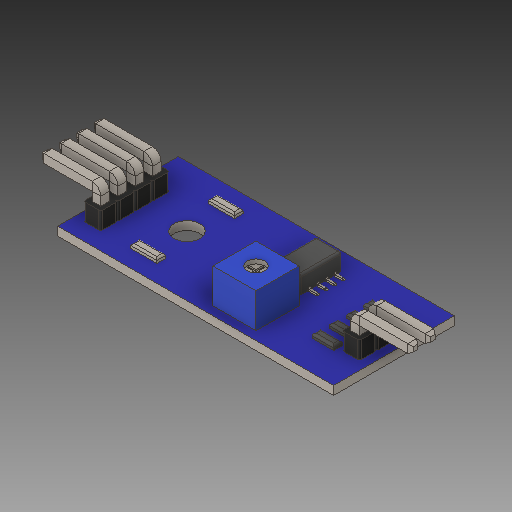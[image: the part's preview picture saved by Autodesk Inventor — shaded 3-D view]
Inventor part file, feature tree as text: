
AUTODESK INVENTOR PART (.ipt)
format: ipt  version: 2017 (Build 210142000, 142)  size: 332,800 bytes
history: native  units: mm
features: fillet x1
ambient origin geometry x8: Origin, YZ Plane, XZ Plane, XY Plane, X Axis, Y Axis, Z Axis, Center Point
bodies: Solid1 (feature_tree)
feature tree (1):
  fillet  "Fillet4"  [1 undecoded]
note: 1 required parameter value undecoded (feature->parameter linkage not recoverable at this tier; creation-order binding heuristic only, values carry confidence <= 0.55)
